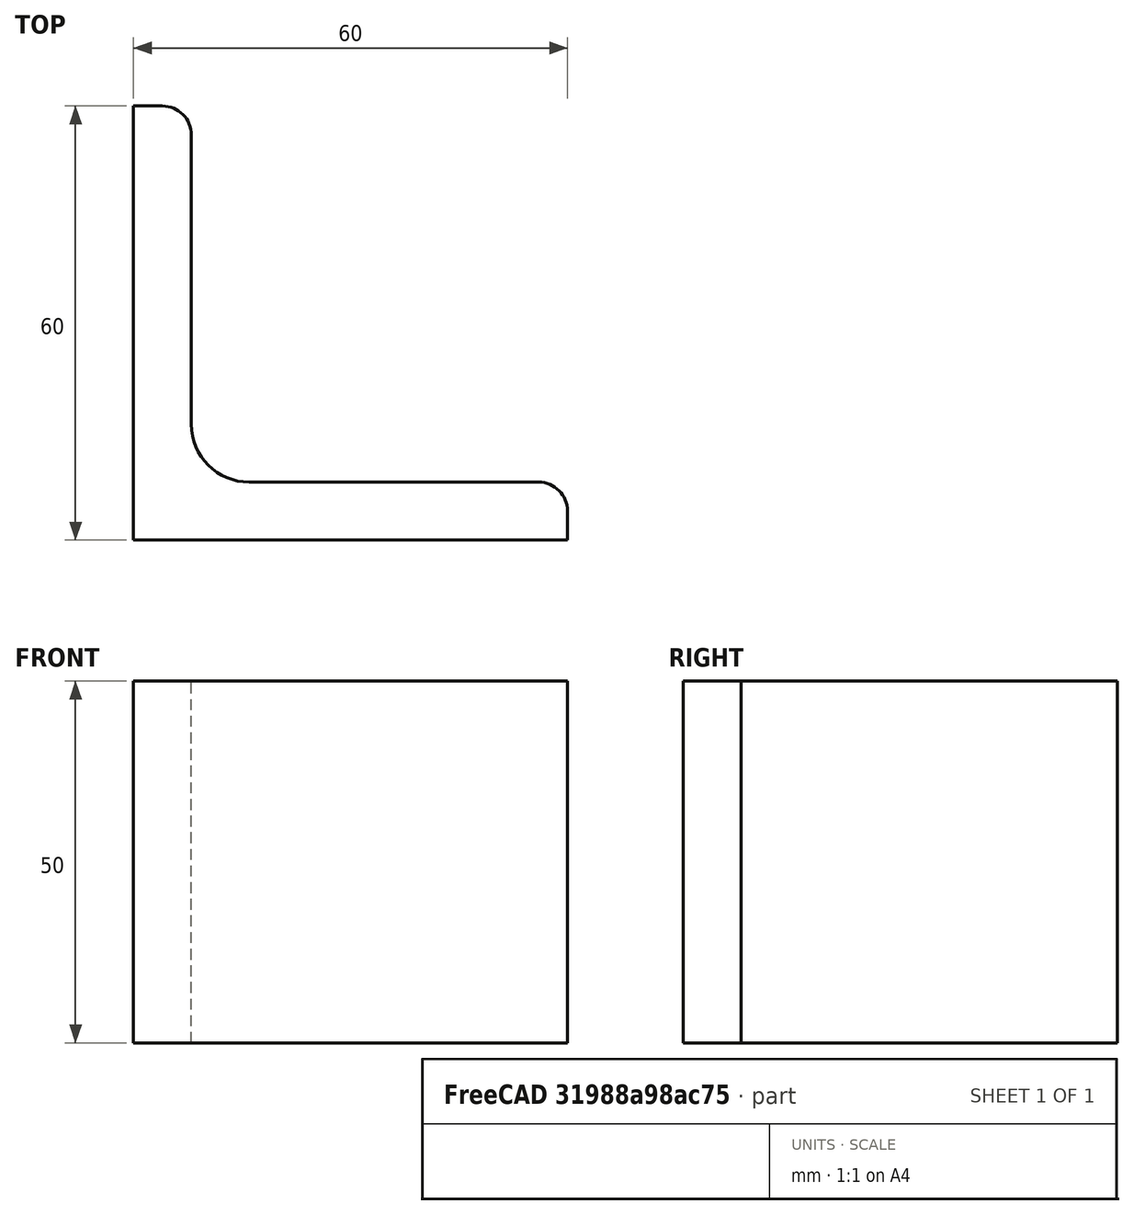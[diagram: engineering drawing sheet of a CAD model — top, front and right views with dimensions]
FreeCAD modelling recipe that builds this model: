
FCSTD DOCUMENT  (FreeCAD 0.15R4671 (Git))
Label: Angle Bar L60x60x8 EN10056 S235JR
License: All rights reserved
LicenseURL: http://en.wikipedia.org/wiki/All_rights_reserved
objects: Sketcher::SketchObject×1, Part::Extrusion×1
note: 2 computed .brp shape members not serialized (recipe doc carries the construction recipe); baked Part::Feature solids carry a one-line shape summary decoded from their .brp

FEATURE [Sketcher::SketchObject] Sketch
  sketch-geometry (9):
    g0: LineSegment StartX=0 StartY=0 StartZ=0 EndX=60 EndY=0 EndZ=0
    g1: LineSegment StartX=60 StartY=0 StartZ=0 EndX=60 EndY=4 EndZ=0
    g2: LineSegment StartX=56 StartY=8 StartZ=0 EndX=16 EndY=8 EndZ=0
    g3: LineSegment StartX=0 StartY=0 StartZ=0 EndX=0 EndY=60 EndZ=0
    g4: LineSegment StartX=0 StartY=60 StartZ=0 EndX=4 EndY=60 EndZ=0
    g5: LineSegment StartX=8 StartY=56 StartZ=0 EndX=8 EndY=16 EndZ=0
    g6: ArcOfCircle CenterX=16 CenterY=16 CenterZ=0 NormalX=0 NormalY=0 NormalZ=1 Radius=8 StartAngle=3.14159 EndAngle=4.71239
    g7: ArcOfCircle CenterX=4 CenterY=56 CenterZ=0 NormalX=0 NormalY=0 NormalZ=1 Radius=4 StartAngle=0 EndAngle=1.5708
    g8: ArcOfCircle CenterX=56 CenterY=4 CenterZ=0 NormalX=0 NormalY=0 NormalZ=1 Radius=4 StartAngle=0 EndAngle=1.5708
  constraints (23):
    c: Coincident(g0,g-1)
    c: Horizontal(g0)
    c: Coincident(g1,g0)
    c: Vertical(g1)
    c: Horizontal(g2)
    c: Coincident(g3,g-1)
    c: Vertical(g3)
    c: Coincident(g4,g3)
    c: Horizontal(g4)
    c: Vertical(g5)
    c: Tangent(g5,g6) = -1.5708
    c: Tangent(g2,g6) = 1.5708
    c: Tangent(g4,g7) = 1.5708
    c: Tangent(g5,g7) = 1.5708
    c: Tangent(g2,g8) = -1.5708
    c: Tangent(g1,g8) = -1.5708
    c: DistanceX(g0) = 60
    c: DistanceY(g3) = 60
    c: DistanceY(g0,g2) = 8
    c: DistanceX(g3,g5) = 8
    c: Radius(g6) = 8
    c: Radius(g8) = 4
    c: Radius(g7) = 4
FEATURE [Part::Extrusion] Extrude  label="Angle Bar L60x60x8 EN10056 S235JR"
  Base = -> Sketch
  Dir = (0,0,50)
  Solid = true
